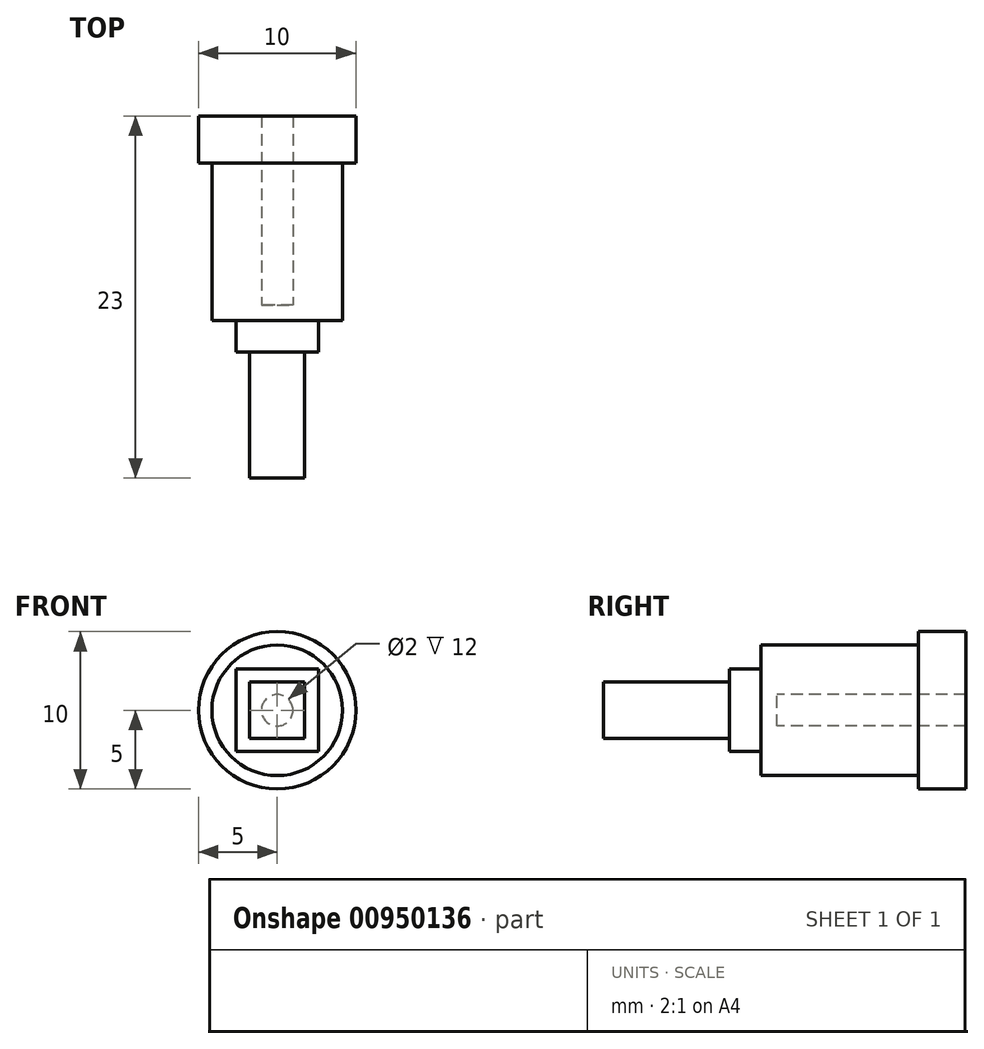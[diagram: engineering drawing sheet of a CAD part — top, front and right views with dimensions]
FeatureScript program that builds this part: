
annotation { "Feature Type Name" : "Feature", "Feature Type Description" : "" }
export const myFeature = defineFeature(function(context is Context, id is Id, definition is map)
    precondition{}
    {
        {
            var Q0;
            Q0=qCreatedBy(makeId("Front.planeOp"),FACE);
            var sketch = newSketch(context, id + "F0", { "sketchPlane" : qUnion([Q0])});
            skCircle(sketch, "E0", {"center": v(0, 0) * mm, "radius": 4.15 * mm});
            skCircle(sketch, "E1", {"center": v(0, 0) * mm, "radius": 1 * mm});
            skCircle(sketch, "E2", {"center": v(0, 0) * mm, "radius": 2.5 * mm});
            skLineSegment(sketch, "E3.bottom", {"start": v(1.75, 1.79) * mm, "end": v(-1.75, 1.79) * mm});
            skLineSegment(sketch, "E3.top", {"start": v(1.75, -1.79) * mm, "end": v(-1.75, -1.79) * mm});
            skLineSegment(sketch, "E3.left", {"start": v(1.75, 1.79) * mm, "end": v(1.75, -1.79) * mm});
            skLineSegment(sketch, "E3.right", {"start": v(-1.75, 1.79) * mm, "end": v(-1.75, -1.79) * mm});
            skCircle(sketch, "E4", {"center": v(0, 0) * mm, "radius": 5 * mm});
            skLineSegment(sketch, "E5.bottom", {"start": v(2.62, 2.62) * mm, "end": v(-2.63, 2.62) * mm});
            skLineSegment(sketch, "E5.top", {"start": v(2.62, -2.62) * mm, "end": v(-2.62, -2.62) * mm});
            skLineSegment(sketch, "E5.left", {"start": v(2.62, 2.62) * mm, "end": v(2.63, -2.62) * mm});
            skLineSegment(sketch, "E5.right", {"start": v(-2.63, 2.62) * mm, "end": v(-2.62, -2.62) * mm});
            skSolve(sketch);
        }
        {
            var Q0;
            Q0=makeQuery(id+"F0.imprint","IMPRINT",FACE,{"disambiguationData":[TD([[makeQuery(id+"F0.imprint","IMPRINT",EDGE,{"derivedFrom":sQuery(id+"F0.wireOp",EDGE,"E1")}),-1.0]])]});
            var Q1;
            Q1=makeQuery(id+"F0.imprint","IMPRINT",FACE,{"disambiguationData":[TD([[makeQuery(id+"F0.imprint","IMPRINT",EDGE,{"derivedFrom":sQuery(id+"F0.wireOp",EDGE,"E1")}),1.0]])]});
            extrude(context, id + "F1", {"entities" : qUnion([Q0, Q1]), "depth" : 11 * mm, "offsetDistance" : 25 * mm});
        }
        {
            var Q0;
            {var subQ2=sQuery(id+"F0.wireOp",EDGE,"E5.bottom");var subQ4=sQuery(id+"F0.wireOp",EDGE,"E5.right");var subQ6=makeQuery(id+"F0.imprint","INTERSECT",VERTEX,{"derivedFrom":[subQ2,subQ4]});Q0=makeQuery(id+"F0.imprint","IMPRINT",FACE,{"disambiguationData":[TD([[makeQuery(id+"F0.imprint","IMPRINT",EDGE,{"disambiguationData":[TD([[subQ6,1.0]])],"derivedFrom":subQ2}),1.0]])]});}
            var Q1;
            {var subQ0=sQuery(id+"F0.wireOp",EDGE,"E3.right");Q1=makeQuery(id+"F0.imprint","IMPRINT",FACE,{"disambiguationData":[TD([[makeQuery(id+"F0.imprint","IMPRINT",EDGE,{"derivedFrom":subQ0}),-1.0]])]});}
            var Q2;
            {var subQ2=sQuery(id+"F0.wireOp",EDGE,"E5.left");var subQ4=sQuery(id+"F0.wireOp",EDGE,"E5.bottom");var subQ6=makeQuery(id+"F0.imprint","INTERSECT",VERTEX,{"derivedFrom":[subQ4,subQ2]});Q2=makeQuery(id+"F0.imprint","IMPRINT",FACE,{"disambiguationData":[TD([[makeQuery(id+"F0.imprint","IMPRINT",EDGE,{"disambiguationData":[TD([[subQ6,-1.0]])],"derivedFrom":subQ4}),1.0]])]});}
            var Q3;
            {var subQ2=sQuery(id+"F0.wireOp",EDGE,"E5.top");var subQ4=sQuery(id+"F0.wireOp",EDGE,"E5.left");var subQ6=makeQuery(id+"F0.imprint","INTERSECT",VERTEX,{"derivedFrom":[subQ2,subQ4]});Q3=makeQuery(id+"F0.imprint","IMPRINT",FACE,{"disambiguationData":[TD([[makeQuery(id+"F0.imprint","IMPRINT",EDGE,{"disambiguationData":[TD([[subQ6,-1.0]])],"derivedFrom":subQ2}),-1.0]])]});}
            var Q4;
            {var subQ2=sQuery(id+"F0.wireOp",EDGE,"E5.right");var subQ4=sQuery(id+"F0.wireOp",EDGE,"E5.top");var subQ6=makeQuery(id+"F0.imprint","INTERSECT",VERTEX,{"derivedFrom":[subQ4,subQ2]});Q4=makeQuery(id+"F0.imprint","IMPRINT",FACE,{"disambiguationData":[TD([[makeQuery(id+"F0.imprint","IMPRINT",EDGE,{"disambiguationData":[TD([[subQ6,1.0]])],"derivedFrom":subQ4}),-1.0]])]});}
            var Q5;
            {var subQ0=sQuery(id+"F0.wireOp",EDGE,"E3.top");Q5=makeQuery(id+"F0.imprint","IMPRINT",FACE,{"disambiguationData":[TD([[makeQuery(id+"F0.imprint","IMPRINT",EDGE,{"derivedFrom":subQ0}),1.0]])]});}
            var Q6;
            {var subQ0=sQuery(id+"F0.wireOp",EDGE,"E3.left");Q6=makeQuery(id+"F0.imprint","IMPRINT",FACE,{"disambiguationData":[TD([[makeQuery(id+"F0.imprint","IMPRINT",EDGE,{"derivedFrom":subQ0}),1.0]])]});}
            var Q7;
            {var subQ0=sQuery(id+"F0.wireOp",EDGE,"E3.bottom");Q7=makeQuery(id+"F0.imprint","IMPRINT",FACE,{"disambiguationData":[TD([[makeQuery(id+"F0.imprint","IMPRINT",EDGE,{"derivedFrom":subQ0}),-1.0]])]});}
            extrude(context, id + "F2", {"entities" : qUnion([Q0, Q1, Q2, Q3, Q4, Q5, Q6, Q7]), "operationType" : NewBodyOperationType.ADD, "depth" : 3 * mm, "offsetDistance" : 25 * mm});
        }
        {
            var Q0;
            Q0=makeQuery(id+"F0.imprint","IMPRINT",FACE,{"disambiguationData":[TD([[makeQuery(id+"F0.imprint","IMPRINT",EDGE,{"derivedFrom":sQuery(id+"F0.wireOp",EDGE,"E0")}),1.0]])]});
            extrude(context, id + "F3", {"entities" : qUnion([Q0]), "operationType" : NewBodyOperationType.ADD, "depth" : -8 * mm, "offsetDistance" : 25 * mm, "hasSecondDirection" : true, "secondDirectionOppositeDirection" : true, "secondDirectionDepth" : -1 * mm});
        }
        {
            var Q0;
            {var subQ2=sQuery(id+"F0.wireOp",EDGE,"E5.left");var subQ4=sQuery(id+"F0.wireOp",EDGE,"E5.bottom");var subQ6=makeQuery(id+"F0.imprint","INTERSECT",VERTEX,{"derivedFrom":[subQ4,subQ2]});Q0=makeQuery(id+"F0.imprint","IMPRINT",FACE,{"disambiguationData":[TD([[makeQuery(id+"F0.imprint","IMPRINT",EDGE,{"disambiguationData":[TD([[subQ6,-1.0]])],"derivedFrom":subQ4}),1.0]])]});}
            var Q1;
            {var subQ0=sQuery(id+"F0.wireOp",EDGE,"E3.bottom");Q1=makeQuery(id+"F0.imprint","IMPRINT",FACE,{"disambiguationData":[TD([[makeQuery(id+"F0.imprint","IMPRINT",EDGE,{"derivedFrom":subQ0}),-1.0]])]});}
            var Q2;
            {var subQ2=sQuery(id+"F0.wireOp",EDGE,"E5.bottom");var subQ4=sQuery(id+"F0.wireOp",EDGE,"E5.right");var subQ6=makeQuery(id+"F0.imprint","INTERSECT",VERTEX,{"derivedFrom":[subQ2,subQ4]});Q2=makeQuery(id+"F0.imprint","IMPRINT",FACE,{"disambiguationData":[TD([[makeQuery(id+"F0.imprint","IMPRINT",EDGE,{"disambiguationData":[TD([[subQ6,1.0]])],"derivedFrom":subQ2}),1.0]])]});}
            var Q3;
            {var subQ0=sQuery(id+"F0.wireOp",EDGE,"E3.right");Q3=makeQuery(id+"F0.imprint","IMPRINT",FACE,{"disambiguationData":[TD([[makeQuery(id+"F0.imprint","IMPRINT",EDGE,{"derivedFrom":subQ0}),-1.0]])]});}
            var Q4;
            {var subQ0=sQuery(id+"F0.wireOp",EDGE,"E3.left");Q4=makeQuery(id+"F0.imprint","IMPRINT",FACE,{"disambiguationData":[TD([[makeQuery(id+"F0.imprint","IMPRINT",EDGE,{"derivedFrom":subQ0}),1.0]])]});}
            var Q5;
            {var subQ2=sQuery(id+"F0.wireOp",EDGE,"E5.top");var subQ4=sQuery(id+"F0.wireOp",EDGE,"E5.left");var subQ6=makeQuery(id+"F0.imprint","INTERSECT",VERTEX,{"derivedFrom":[subQ2,subQ4]});Q5=makeQuery(id+"F0.imprint","IMPRINT",FACE,{"disambiguationData":[TD([[makeQuery(id+"F0.imprint","IMPRINT",EDGE,{"disambiguationData":[TD([[subQ6,-1.0]])],"derivedFrom":subQ2}),-1.0]])]});}
            var Q6;
            {var subQ2=sQuery(id+"F0.wireOp",EDGE,"E5.right");var subQ4=sQuery(id+"F0.wireOp",EDGE,"E5.top");var subQ6=makeQuery(id+"F0.imprint","INTERSECT",VERTEX,{"derivedFrom":[subQ4,subQ2]});Q6=makeQuery(id+"F0.imprint","IMPRINT",FACE,{"disambiguationData":[TD([[makeQuery(id+"F0.imprint","IMPRINT",EDGE,{"disambiguationData":[TD([[subQ6,1.0]])],"derivedFrom":subQ4}),-1.0]])]});}
            var Q7;
            {var subQ0=sQuery(id+"F0.wireOp",EDGE,"E3.top");Q7=makeQuery(id+"F0.imprint","IMPRINT",FACE,{"disambiguationData":[TD([[makeQuery(id+"F0.imprint","IMPRINT",EDGE,{"derivedFrom":subQ0}),1.0]])]});}
            var Q8;
            Q8=makeQuery(id+"F0.imprint","IMPRINT",FACE,{"disambiguationData":[TD([[makeQuery(id+"F0.imprint","IMPRINT",EDGE,{"derivedFrom":sQuery(id+"F0.wireOp",EDGE,"E1")}),-1.0]])]});
            extrude(context, id + "F4", {"entities" : qUnion([Q0, Q1, Q2, Q3, Q4, Q5, Q6, Q7, Q8]), "operationType" : NewBodyOperationType.ADD, "depth" : -12 * mm, "offsetDistance" : 25 * mm});
        }
        {
            var Q0;
            Q0=makeQuery(id+"F3.opExtrude","CAP_FACE",FACE,{"disambiguationData":[OSD([sQuery(id+"F0.wireOp",EDGE,"E0"),sQuery(id+"F0.wireOp",EDGE,"E5.bottom"),sQuery(id+"F0.wireOp",EDGE,"E5.top"),sQuery(id+"F0.wireOp",EDGE,"E5.left"),sQuery(id+"F0.wireOp",EDGE,"E5.right")])],"isStart":false});
            extrude(context, id + "F5", {"entities" : qUnion([Q0]), "operationType" : NewBodyOperationType.ADD, "depth" : 4 * mm, "offsetDistance" : 25 * mm});
        }
        {
            var Q0;
            Q0=makeQuery(id+"F0.imprint","IMPRINT",FACE,{"disambiguationData":[TD([[makeQuery(id+"F0.imprint","IMPRINT",EDGE,{"derivedFrom":sQuery(id+"F0.wireOp",EDGE,"E0")}),-1.0]])]});
            extrude(context, id + "F6", {"entities" : qUnion([Q0]), "operationType" : NewBodyOperationType.ADD, "depth" : -12 * mm, "offsetDistance" : 25 * mm, "hasSecondDirection" : true, "secondDirectionOppositeDirection" : true, "secondDirectionDepth" : 9 * mm});
        }
    });
